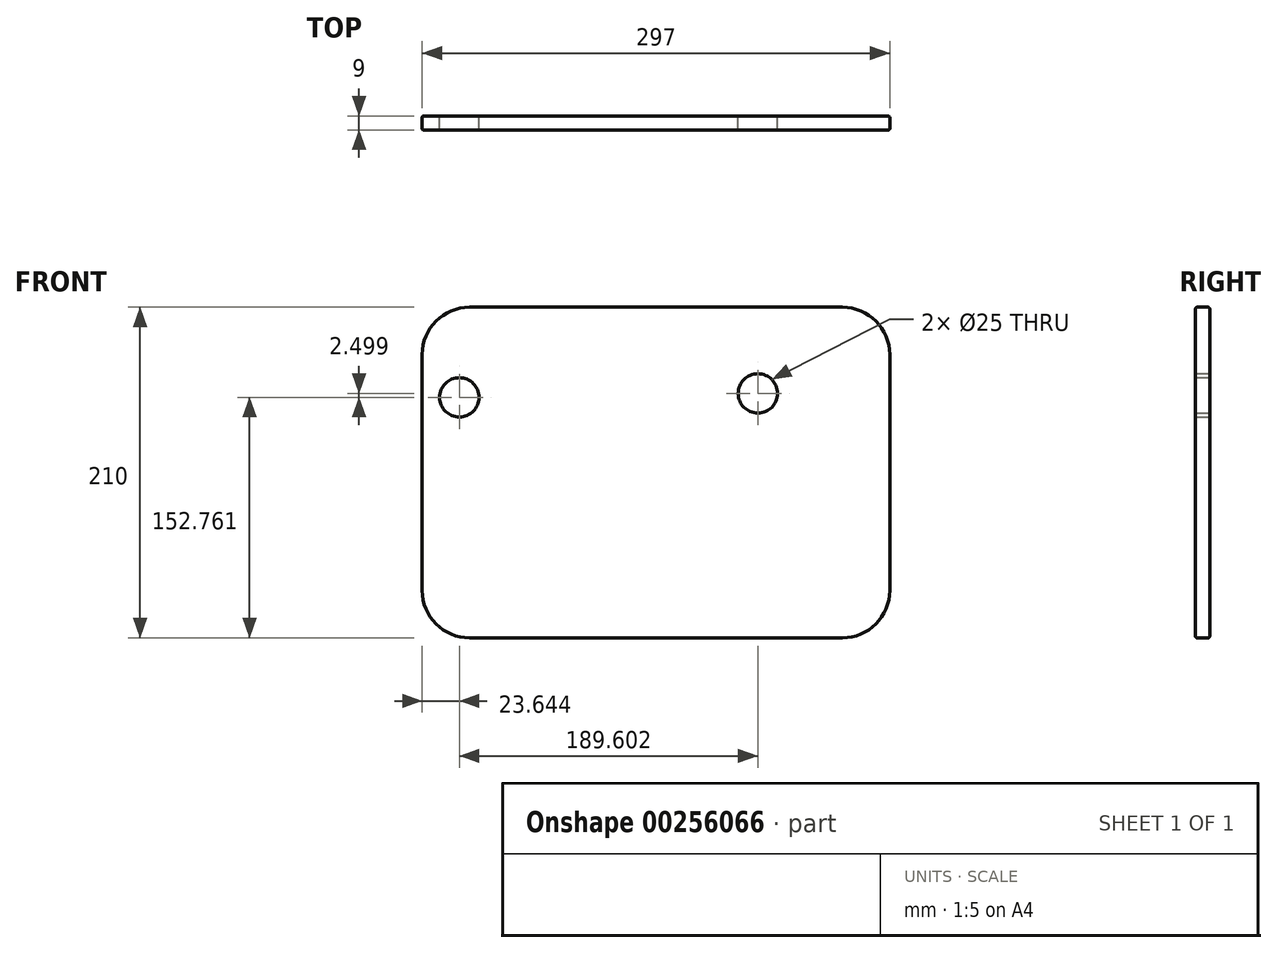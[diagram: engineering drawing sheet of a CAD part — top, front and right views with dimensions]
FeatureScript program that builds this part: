
annotation { "Feature Type Name" : "Feature", "Feature Type Description" : "" }
export const myFeature = defineFeature(function(context is Context, id is Id, definition is map)
    precondition{}
    {
        {
            var Q0;
            Q0=qCreatedBy(makeId("Front.planeOp"),FACE);
            var sketch = newSketch(context, id + "F0", { "sketchPlane" : qUnion([Q0])});
            skLineSegment(sketch, "E0.bottom", {"start": v(-121.78, 151.1) * mm, "end": v(115.22, 151.1) * mm});
            skLineSegment(sketch, "E0.top", {"start": v(-121.78, -58.9) * mm, "end": v(115.22, -58.9) * mm});
            skLineSegment(sketch, "E0.left", {"start": v(-151.78, 121.1) * mm, "end": v(-151.78, -28.9) * mm});
            skLineSegment(sketch, "E0.right", {"start": v(145.22, 121.1) * mm, "end": v(145.22, -28.9) * mm});
            skPoint(sketch, "E1.visualSharp", {"position": v(-151.78, 151.1) * mm});
            skArc(sketch, "E1.filletArc", {"start": v(-121.78, 151.1) * mm, "mid": v(-143, 142.31) * mm, "end": v(-151.78, 121.1) * mm});
            skPoint(sketch, "E2.visualSharp", {"position": v(145.22, 151.1) * mm});
            skArc(sketch, "E2.filletArc", {"start": v(145.22, 121.1) * mm, "mid": v(136.44, 142.31) * mm, "end": v(115.22, 151.1) * mm});
            skPoint(sketch, "E3.visualSharp", {"position": v(145.22, -58.9) * mm});
            skArc(sketch, "E3.filletArc", {"start": v(115.22, -58.9) * mm, "mid": v(136.44, -50.11) * mm, "end": v(145.22, -28.9) * mm});
            skPoint(sketch, "E4.visualSharp", {"position": v(-151.78, -58.9) * mm});
            skArc(sketch, "E4.filletArc", {"start": v(-151.78, -28.9) * mm, "mid": v(-143, -50.11) * mm, "end": v(-121.78, -58.9) * mm});
            skCircle(sketch, "E5", {"center": v(-128.14, 93.86) * mm, "radius": 12.5 * mm});
            skCircle(sketch, "E6", {"center": v(61.47, 96.36) * mm, "radius": 12.5 * mm});
            skSolve(sketch);
        }
        {
            var Q0;
            Q0 = qSketchRegion(id + "F0", true);
            extrude(context, id + "F1", {"entities" : qUnion([Q0]), "depth" : 9 * mm});
        }
        {
            var Q0;
            Q0=makeQuery(id+"F1.opExtrude","CAP_FACE",FACE,{"disambiguationData":[OSD([sQuery(id+"F0.wireOp",EDGE,"E0.bottom"),sQuery(id+"F0.wireOp",EDGE,"E0.top"),sQuery(id+"F0.wireOp",EDGE,"E0.left"),sQuery(id+"F0.wireOp",EDGE,"E0.right"),sQuery(id+"F0.wireOp",EDGE,"E1.filletArc"),sQuery(id+"F0.wireOp",EDGE,"E2.filletArc"),sQuery(id+"F0.wireOp",EDGE,"E3.filletArc"),sQuery(id+"F0.wireOp",EDGE,"E4.filletArc"),sQuery(id+"F0.wireOp",EDGE,"E5"),sQuery(id+"F0.wireOp",EDGE,"E6")])],"isStart":true});
            var Q1;
            Q1=makeQuery(id+"F1.opExtrude","CAP_FACE",FACE,{"disambiguationData":[OSD([sQuery(id+"F0.wireOp",EDGE,"E0.bottom"),sQuery(id+"F0.wireOp",EDGE,"E0.top"),sQuery(id+"F0.wireOp",EDGE,"E0.left"),sQuery(id+"F0.wireOp",EDGE,"E0.right"),sQuery(id+"F0.wireOp",EDGE,"E1.filletArc"),sQuery(id+"F0.wireOp",EDGE,"E2.filletArc"),sQuery(id+"F0.wireOp",EDGE,"E3.filletArc"),sQuery(id+"F0.wireOp",EDGE,"E4.filletArc"),sQuery(id+"F0.wireOp",EDGE,"E5"),sQuery(id+"F0.wireOp",EDGE,"E6")])],"isStart":false});
            fillet(context, id + "F2", {"entities" : qUnion([Q0, Q1]), "radius" : 1 * mm, "tangentPropagation" : true, "allowEdgeOverflow" : false});
        }
    });
